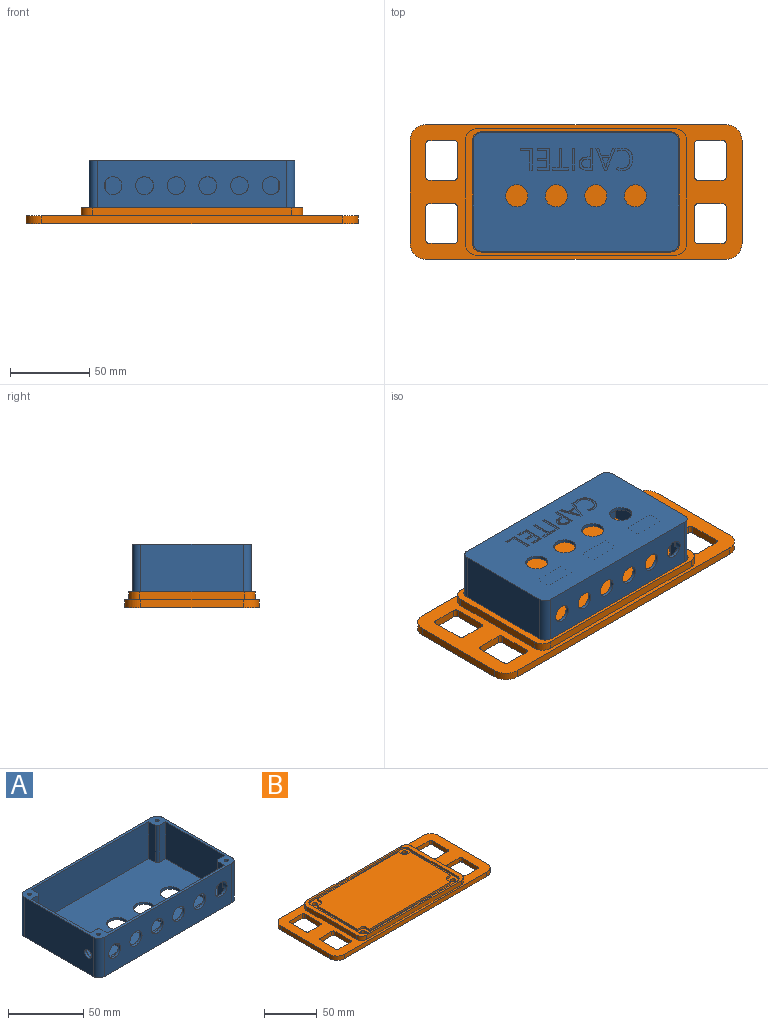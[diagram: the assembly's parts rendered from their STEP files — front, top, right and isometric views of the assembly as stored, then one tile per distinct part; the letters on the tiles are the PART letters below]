
ASSEMBLY  parts=2 mates=1
PART A: 147 faces, bbox 130x75x32 mm
  f0: plane 130x75mm, normal (0,0,-1), area 8800.8mm2, adj f16,f17,f18,f19,f20,f21,f22,f23
  f1: plane 9.5x1.5mm, normal (1,0,0), area 14.2mm2, adj f2,f4,f48,f64
  f2: plane 20.5x1.5mm, normal (0,-1,0), area 30.8mm2, adj f1,f3,f48,f64
  f3: plane 9.5x1.5mm, normal (-1,0,0), area 14.2mm2, adj f2,f4,f48,f64
  f4: plane 20.5x1.5mm, normal (0,1,0), area 30.8mm2, adj f1,f3,f48,f64
  f5: plane 9.5x1.5mm, normal (1,0,0), area 14.2mm2, adj f6,f8,f48,f63
  f6: plane 20.5x1.5mm, normal (0,-1,0), area 30.7mm2, adj f5,f7,f48,f63
  f7: plane 9.5x1.5mm, normal (-1,0,0), area 14.2mm2, adj f6,f8,f48,f63
  f8: plane 20.5x1.5mm, normal (0,1,0), area 30.7mm2, adj f5,f7,f48,f63
  f9: plane 9.5x1.5mm, normal (1,0,0), area 14.2mm2, adj f10,f12,f48,f62
  f10: plane 20.5x1.5mm, normal (0,-1,0), area 30.7mm2, adj f9,f11,f48,f62
  f11: plane 9.5x1.5mm, normal (-1,0,0), area 14.2mm2, adj f10,f12,f48,f62
  f12: plane 20.5x1.5mm, normal (0,1,0), area 30.7mm2, adj f9,f11,f48,f62
  f13: plane 10.75x6mm, normal (0,1,0), area 64.5mm2, adj f14,f33,f48,f61
  f14: cylinder r=2mm len=11.44mm, axis (0,0,-1), area 34.2mm2, adj f13,f36,f48,f61
  f15: plane 130x75mm, normal (0,0,1), area 1015.5mm2, adj f16,f17,f18,f19,f20,f21,f22,f23
  f16: cylinder r=5mm len=32mm, axis (0,0,-1), area 251.3mm2, adj f0,f15,f17,f23
  f17: plane 65x32mm, normal (-1,0,0), area 2046.8mm2, adj f0,f15,f16,f18,f61
  f18: cylinder r=5mm len=32mm, axis (0,0,-1), area 251.3mm2, adj f0,f15,f17,f19
  f19: plane 120x32mm, normal (0,-1,0), area 3238.3mm2, adj f0,f15,f18,f20,f49,f51,f52,f53
  f20: cylinder r=5mm len=32mm, axis (0,0,-1), area 251.3mm2, adj f0,f15,f19,f21
  f21: plane 65x32mm, normal (1,0,0), area 2080mm2, adj f0,f15,f20,f22
  f22: cylinder r=5mm len=32mm, axis (0,0,-1), area 251.3mm2, adj f0,f15,f21,f23
  f23: plane 120x32mm, normal (0,1,0), area 3840mm2, adj f0,f15,f16,f22
  f24: plane 30x6mm, normal (0,1,0), area 180mm2, adj f15,f25,f39,f48
  f25: plane 55x30mm, normal (-1,0,0), area 1650mm2, adj f15,f24,f26,f48
  f26: plane 30x6mm, normal (0,-1,0), area 180mm2, adj f15,f25,f27,f48
  f27: cylinder r=2mm len=30mm, axis (0,0,-1), area 94.2mm2, adj f15,f26,f28,f48
  f28: plane 30x6mm, normal (-1,0,0), area 180mm2, adj f15,f27,f29,f48
  f29: plane 110x30mm, normal (0,-1,0), area 3300mm2, adj f15,f28,f30,f48
  f30: plane 30x6mm, normal (1,0,0), area 180mm2, adj f15,f29,f31,f48
  f31: cylinder r=2mm len=30mm, axis (0,0,-1), area 94.2mm2, adj f15,f30,f32,f48
  f32: plane 30x6mm, normal (0,-1,0), area 180mm2, adj f15,f31,f33,f48
  f33: plane 55x30mm, normal (1,0,0), area 1633.4mm2, adj f13,f15,f32,f34,f48,f61
  f34: plane 12.75x6mm, normal (0,1,0), area 76.5mm2, adj f15,f33,f35,f61
  f35: cylinder r=2mm len=13.44mm, axis (0,0,-1), area 40.5mm2, adj f15,f34,f36,f61
  f36: plane 30x6mm, normal (1,0,0), area 165mm2, adj f14,f15,f35,f37,f48,f49,f50,f61
  f37: plane 110x30mm, normal (0,1,0), area 2702.9mm2, adj f15,f36,f38,f48,f49,f51,f52,f53
  f38: plane 30x6mm, normal (-1,0,0), area 169.5mm2, adj f15,f37,f39,f48,f55,f56
  f39: cylinder r=2mm len=30mm, axis (0,0,-1), area 94.2mm2, adj f15,f24,f38,f48
  f40: cylinder r=1.25mm len=30mm, axis (0,0,-1), area 235.6mm2, adj f15,f47
  f41: cylinder r=1.25mm len=30mm, axis (0,0,-1), area 235.6mm2, adj f15,f46
  f42: cylinder r=1.25mm len=30mm, axis (0,0,-1), area 235.6mm2, adj f15,f45
  f43: cylinder r=1.25mm len=30mm, axis (0,0,-1), area 235.6mm2, adj f15,f44
  f44: plane 2.5x2.5mm, normal (0,0,1), area 4.9mm2, adj f43
  f45: plane 2.5x2.5mm, normal (0,0,1), area 4.9mm2, adj f42
  f46: plane 2.5x2.5mm, normal (0,0,1), area 4.9mm2, adj f41
  f47: plane 2.5x2.5mm, normal (0,0,1), area 4.9mm2, adj f40
  f48: plane 126x71mm, normal (0,0,1), area 7493.4mm2, adj f1,f2,f3,f4,f5,f6,f7,f8
  f49: cylinder r=5.65mm len=11.3mm, axis (0,-1,0), area 81.9mm2, adj f19,f36,f37,f50
  f50: plane 5.26x0.65mm, normal (0,-1,0), area 2.3mm2, adj f36,f49
  f51: cylinder r=5.65mm len=11.3mm, axis (0,-1,0), area 71mm2, adj f19,f37
  f52: cylinder r=5.65mm len=11.3mm, axis (0,-1,0), area 71mm2, adj f19,f37
  f53: cylinder r=5.65mm len=11.3mm, axis (0,-1,0), area 71mm2, adj f19,f37
  f54: cylinder r=5.65mm len=11.3mm, axis (0,-1,0), area 71mm2, adj f19,f37
  f55: cylinder r=5.65mm len=11.3mm, axis (0,-1,0), area 81.9mm2, adj f19,f37,f38,f56
  f56: plane 5.26x0.65mm, normal (0,-1,0), area 2.3mm2, adj f38,f55
  f57: cylinder r=7mm len=14mm, axis (0,0,1), area 88mm2, adj f0,f48
  f58: cylinder r=7mm len=14mm, axis (0,0,1), area 88mm2, adj f0,f48
  f59: cylinder r=7mm len=14mm, axis (0,0,1), area 88mm2, adj f0,f48
  f60: cylinder r=7mm len=14mm, axis (0,0,1), area 88mm2, adj f0,f48
  f61: cylinder r=3.25mm len=10mm, axis (-1,0,0), area 120.8mm2, adj f13,f14,f17,f33,f34,f35,f36
  f62: plane 20.5x9.5mm, normal (0,0,1), area 194.7mm2, adj f9,f10,f11,f12
  f63: plane 20.5x9.5mm, normal (0,0,1), area 194.7mm2, adj f5,f6,f7,f8
  f64: plane 20.5x9.5mm, normal (0,0,1), area 194.8mm2, adj f1,f2,f3,f4
  f65: extruded ~5.16x4.01mm, area 3.7mm2, adj f0,f66,f79,f80
  f66: plane 3.57x0.5mm, normal (0,1,0), area 1.8mm2, adj f0,f65,f67,f80
  f67: plane 13.77x0.5mm, normal (1,0,0), area 6.9mm2, adj f0,f66,f68,f80
  f68: plane 1.6x0.5mm, normal (0,-1,0), area 0.8mm2, adj f0,f67,f69,f80
  f69: plane 5.41x0.5mm, normal (-1,0,0), area 2.7mm2, adj f0,f68,f70,f80
  f70: plane 1.62x0.5mm, normal (0,-1,0), area 0.8mm2, adj f0,f69,f71,f80
  f71: extruded ~4.08x1.13mm, area 2.2mm2, adj f0,f70,f79,f80
  f72: plane 5.59x0.5mm, normal (-1,0,0), area 2.8mm2, adj f73,f78,f80,f81
  f73: plane 1.79x0.5mm, normal (0,-1,0), area 0.9mm2, adj f72,f74,f80,f81
  f74: extruded ~2.79x0.67mm, area 1.5mm2, adj f73,f75,f80,f81
  f75: extruded ~2.03x0.89mm, area 1.2mm2, adj f74,f76,f80,f81
  f76: extruded ~2.21x0.95mm, area 1.2mm2, adj f75,f77,f80,f81
  f77: extruded ~3.08x0.69mm, area 1.6mm2, adj f76,f78,f80,f81
  f78: plane 1.44x0.5mm, normal (0,1,0), area 0.7mm2, adj f72,f77,f80,f81
  f79: extruded ~3.22x1.43mm, area 1.8mm2, adj f0,f65,f71,f80
  f80: plane 13.77x8.73mm, normal (0,0,-1), area 46.7mm2, adj f65,f66,f67,f68,f69,f70,f71,f72
  f81: plane 5.59x5.47mm, normal (0,0,-1), area 27.2mm2, adj f72,f73,f74,f75,f76,f77,f78
  f82: plane 1.66x0.5mm, normal (0,-1,0), area 0.8mm2, adj f0,f83,f94,f95
  f83: plane 13.82x5.41mm, normal (-0.93,0.36,0), area 7.4mm2, adj f0,f82,f84,f95
  f84: plane 1.35x0.5mm, normal (0,1,0), area 0.7mm2, adj f0,f83,f85,f95
  f85: plane 13.82x5.44mm, normal (0.93,0.37,0), area 7.4mm2, adj f0,f84,f86,f95
  f86: plane 1.62x0.5mm, normal (0,-1,0), area 0.8mm2, adj f0,f85,f87,f95
  f87: plane 4.38x1.69mm, normal (-0.93,-0.36,0), area 2.3mm2, adj f0,f86,f88,f95
  f88: plane 5.52x0.5mm, normal (0,-1,0), area 2.8mm2, adj f0,f87,f94,f95
  f89: plane 4.45x0.5mm, normal (0,1,0), area 2.2mm2, adj f90,f93,f95,f96
  f90: plane 4.27x1.62mm, normal (-0.94,-0.35,0), area 2.3mm2, adj f89,f91,f95,f96
  f91: extruded ~1.99x0.59mm, area 1mm2, adj f90,f92,f95,f96
  f92: extruded ~1.99x0.64mm, area 1mm2, adj f91,f93,f95,f96
  f93: plane 4.27x1.6mm, normal (0.94,-0.35,0), area 2.3mm2, adj f89,f92,f95,f96
  f94: plane 4.38x1.71mm, normal (0.93,-0.36,0), area 2.4mm2, adj f0,f82,f88,f95
  f95: plane 13.82x12.2mm, normal (0,0,-1), area 48.8mm2, adj f82,f83,f84,f85,f86,f87,f88,f89
  f96: plane 6.25x4.45mm, normal (0,0,-1), area 13.3mm2, adj f89,f90,f91,f92,f93
  f97: plane 7.67x0.5mm, normal (0,-1,0), area 3.8mm2, adj f0,f98,f102,f103
  f98: plane 1.45x0.5mm, normal (-1,0,0), area 0.7mm2, adj f0,f97,f99,f103
  f99: plane 6.07x0.5mm, normal (0,1,0), area 3mm2, adj f0,f98,f100,f103
  f100: plane 12.32x0.5mm, normal (-1,0,0), area 6.2mm2, adj f0,f99,f101,f103
  f101: plane 1.6x0.5mm, normal (0,1,0), area 0.8mm2, adj f0,f100,f102,f103
  f102: plane 13.77x0.5mm, normal (1,0,0), area 6.9mm2, adj f0,f97,f101,f103
  f103: plane 13.77x7.67mm, normal (0,0,-1), area 30.8mm2, adj f97,f98,f99,f100,f101,f102
  f104: plane 1.43x0.5mm, normal (-1,0,0), area 0.7mm2, adj f0,f105,f115,f116
  f105: plane 6.07x0.5mm, normal (0,1,0), area 3mm2, adj f0,f104,f106,f116
  f106: plane 5.06x0.5mm, normal (-1,0,0), area 2.5mm2, adj f0,f105,f107,f116
  f107: plane 5.71x0.5mm, normal (0,-1,0), area 2.9mm2, adj f0,f106,f108,f116
  f108: plane 1.41x0.5mm, normal (-1,0,0), area 0.7mm2, adj f0,f107,f109,f116
  f109: plane 5.71x0.5mm, normal (0,1,0), area 2.9mm2, adj f0,f108,f110,f116
  f110: plane 4.43x0.5mm, normal (-1,0,0), area 2.2mm2, adj f0,f109,f111,f116
  f111: plane 6.07x0.5mm, normal (0,-1,0), area 3mm2, adj f0,f110,f112,f116
  f112: plane 1.42x0.5mm, normal (-1,0,0), area 0.7mm2, adj f0,f111,f113,f116
  f113: plane 7.67x0.5mm, normal (0,1,0), area 3.8mm2, adj f0,f112,f114,f116
  f114: plane 13.77x0.5mm, normal (1,0,0), area 6.9mm2, adj f0,f113,f115,f116
  f115: plane 7.67x0.5mm, normal (0,-1,0), area 3.8mm2, adj f0,f104,f114,f116
  f116: plane 13.77x7.67mm, normal (0,0,-1), area 47.4mm2, adj f104,f105,f106,f107,f108,f109,f110,f111
  f117: plane 12.34x0.5mm, normal (-1,0,0), area 6.2mm2, adj f0,f118,f124,f125
  f118: plane 4.36x0.5mm, normal (0,-1,0), area 2.2mm2, adj f0,f117,f119,f125
  f119: plane 1.42x0.5mm, normal (-1,0,0), area 0.7mm2, adj f0,f118,f120,f125
  f120: plane 10.32x0.5mm, normal (0,1,0), area 5.2mm2, adj f0,f119,f121,f125
  f121: plane 1.42x0.5mm, normal (1,0,0), area 0.7mm2, adj f0,f120,f122,f125
  f122: plane 4.36x0.5mm, normal (0,-1,0), area 2.2mm2, adj f0,f121,f123,f125
  f123: plane 12.34x0.5mm, normal (1,0,0), area 6.2mm2, adj f0,f122,f124,f125
  f124: plane 1.6x0.5mm, normal (0,-1,0), area 0.8mm2, adj f0,f117,f123,f125
  f125: plane 13.77x10.32mm, normal (0,0,-1), area 34.4mm2, adj f117,f118,f119,f120,f121,f122,f123,f124
  f126: plane 1.6x0.5mm, normal (0,-1,0), area 0.8mm2, adj f0,f127,f129,f130
  f127: plane 13.77x0.5mm, normal (-1,0,0), area 6.9mm2, adj f0,f126,f128,f130
  f128: plane 1.6x0.5mm, normal (0,1,0), area 0.8mm2, adj f0,f127,f129,f130
  f129: plane 13.77x0.5mm, normal (1,0,0), area 6.9mm2, adj f0,f126,f128,f130
  f130: plane 13.77x1.6mm, normal (0,0,-1), area 22mm2, adj f126,f127,f128,f129
  f131: extruded ~3.13x0.73mm, area 1.6mm2, adj f0,f132,f145,f146
  f132: plane 1.37x0.68mm, normal (-0.9,-0.44,0), area 0.8mm2, adj f0,f131,f133,f146
  f133: extruded ~3.78x0.79mm, area 1.9mm2, adj f0,f132,f134,f146
  f134: extruded ~3.54x0.87mm, area 1.8mm2, adj f0,f133,f135,f146
  f135: extruded ~2.47x2.3mm, area 1.7mm2, adj f0,f134,f136,f146
  f136: extruded ~3.73x0.8mm, area 1.9mm2, adj f0,f135,f137,f146
  f137: extruded ~5.25x1.65mm, area 2.8mm2, adj f0,f136,f138,f146
  f138: extruded ~4.69x1.85mm, area 2.6mm2, adj f0,f137,f139,f146
  f139: extruded ~3.53x0.54mm, area 1.8mm2, adj f0,f138,f140,f146
  f140: plane 1.4x0.5mm, normal (-1,0,0), area 0.7mm2, adj f0,f139,f141,f146
  f141: extruded ~3.29x0.52mm, area 1.7mm2, adj f0,f140,f142,f146
  f142: extruded ~3.61x1.47mm, area 2mm2, adj f0,f141,f143,f146
  f143: extruded ~4.17x1.27mm, area 2.2mm2, adj f0,f142,f144,f146
  f144: extruded ~4.14x1.31mm, area 2.2mm2, adj f0,f143,f145,f146
  f145: extruded ~3.58x1.51mm, area 2mm2, adj f0,f131,f144,f146
  f146: plane 14.15x10.41mm, normal (0,0,-1), area 41.4mm2, adj f131,f132,f133,f134,f135,f136,f137,f138
PART B: 81 faces, bbox 210x85x10 mm
  f0: plane 210x85mm, normal (0,0,1), area 4620mm2, adj f2,f3,f4,f5,f6,f7,f8,f9
  f1: plane 210x85mm, normal (0,0,-1), area 15699.4mm2, adj f2,f3,f4,f5,f6,f7,f8,f9
  f2: cylinder r=10mm len=10mm, axis (0,0,-1), area 78.5mm2, adj f0,f1,f3,f9
  f3: plane 190x5mm, normal (0,1,0), area 950mm2, adj f0,f1,f2,f4
  f4: cylinder r=10mm len=10mm, axis (0,0,-1), area 78.5mm2, adj f0,f1,f3,f5
  f5: plane 65x5mm, normal (-1,0,0), area 325mm2, adj f0,f1,f4,f6
  f6: cylinder r=10mm len=10mm, axis (0,0,-1), area 78.5mm2, adj f0,f1,f5,f7
  f7: plane 190x5mm, normal (0,-1,0), area 950mm2, adj f0,f1,f6,f8
  f8: cylinder r=10mm len=10mm, axis (0,0,-1), area 78.5mm2, adj f0,f1,f7,f9
  f9: plane 65x5mm, normal (1,0,0), area 325mm2, adj f0,f1,f2,f8
  f10: cylinder r=2mm len=5mm, axis (0,0,-1), area 15.7mm2, adj f0,f1,f11,f17
  f11: plane 21x5mm, normal (1,0,0), area 105mm2, adj f0,f1,f10,f12
  f12: cylinder r=2mm len=5mm, axis (0,0,-1), area 15.7mm2, adj f0,f1,f11,f13
  f13: plane 16x5mm, normal (0,1,0), area 80mm2, adj f0,f1,f12,f14
  f14: cylinder r=2mm len=5mm, axis (0,0,-1), area 15.7mm2, adj f0,f1,f13,f15
  f15: plane 21x5mm, normal (-1,0,0), area 105mm2, adj f0,f1,f14,f16
  f16: cylinder r=2mm len=5mm, axis (0,0,-1), area 15.7mm2, adj f0,f1,f15,f17
  f17: plane 16x5mm, normal (0,-1,0), area 80mm2, adj f0,f1,f10,f16
  f18: cylinder r=2mm len=5mm, axis (0,0,-1), area 15.7mm2, adj f0,f1,f19,f25
  f19: plane 21x5mm, normal (-1,0,0), area 105mm2, adj f0,f1,f18,f20
  f20: cylinder r=2mm len=5mm, axis (0,0,-1), area 15.7mm2, adj f0,f1,f19,f21
  f21: plane 16x5mm, normal (0,-1,0), area 80mm2, adj f0,f1,f20,f22
  f22: cylinder r=2mm len=5mm, axis (0,0,-1), area 15.7mm2, adj f0,f1,f21,f23
  f23: plane 21x5mm, normal (1,0,0), area 105mm2, adj f0,f1,f22,f24
  f24: cylinder r=2mm len=5mm, axis (0,0,-1), area 15.7mm2, adj f0,f1,f23,f25
  f25: plane 16x5mm, normal (0,1,0), area 80mm2, adj f0,f1,f18,f24
  f26: cylinder r=2mm len=5mm, axis (0,0,-1), area 15.7mm2, adj f0,f1,f27,f33
  f27: plane 21x5mm, normal (-1,0,0), area 105mm2, adj f0,f1,f26,f28
  f28: cylinder r=2mm len=5mm, axis (0,0,-1), area 15.7mm2, adj f0,f1,f27,f29
  f29: plane 16x5mm, normal (0,-1,0), area 80mm2, adj f0,f1,f28,f30
  f30: cylinder r=2mm len=5mm, axis (0,0,-1), area 15.7mm2, adj f0,f1,f29,f31
  f31: plane 21x5mm, normal (1,0,0), area 105mm2, adj f0,f1,f30,f32
  f32: cylinder r=2mm len=5mm, axis (0,0,-1), area 15.7mm2, adj f0,f1,f31,f33
  f33: plane 16x5mm, normal (0,1,0), area 80mm2, adj f0,f1,f26,f32
  f34: cylinder r=2mm len=5mm, axis (0,0,-1), area 15.7mm2, adj f0,f1,f35,f41
  f35: plane 16x5mm, normal (0,-1,0), area 80mm2, adj f0,f1,f34,f36
  f36: cylinder r=2mm len=5mm, axis (0,0,-1), area 15.7mm2, adj f0,f1,f35,f37
  f37: plane 21x5mm, normal (1,0,0), area 105mm2, adj f0,f1,f36,f38
  f38: cylinder r=2mm len=5mm, axis (0,0,-1), area 15.7mm2, adj f0,f1,f37,f39
  f39: plane 16x5mm, normal (0,1,0), area 80mm2, adj f0,f1,f38,f40
  f40: cylinder r=2mm len=5mm, axis (0,0,-1), area 15.7mm2, adj f0,f1,f39,f41
  f41: plane 21x5mm, normal (-1,0,0), area 105mm2, adj f0,f1,f34,f40
  f42: cylinder r=2.5mm len=8mm, axis (0,0,-1), area 125.7mm2, adj f1,f63
  f43: cylinder r=2.5mm len=8mm, axis (0,0,-1), area 125.7mm2, adj f1,f63
  f44: cylinder r=2.5mm len=8mm, axis (0,0,-1), area 125.7mm2, adj f1,f63
  f45: cylinder r=2.5mm len=8mm, axis (0,0,-1), area 125.7mm2, adj f1,f63
  f46: cylinder r=7mm len=7mm, axis (0,0,-1), area 55mm2, adj f0,f47,f53,f54
  f47: plane 126x5mm, normal (0,-1,0), area 630mm2, adj f0,f46,f48,f54
  f48: cylinder r=7mm len=7mm, axis (0,0,-1), area 55mm2, adj f0,f47,f49,f54
  f49: plane 66x5mm, normal (1,0,0), area 330mm2, adj f0,f48,f50,f54
  f50: cylinder r=7mm len=7mm, axis (0,0,-1), area 55mm2, adj f0,f49,f51,f54
  f51: plane 126x5mm, normal (0,1,0), area 630mm2, adj f0,f50,f52,f54
  f52: cylinder r=7mm len=7mm, axis (0,0,-1), area 55mm2, adj f0,f51,f53,f54
  f53: plane 66x5mm, normal (-1,0,0), area 330mm2, adj f0,f46,f52,f54
  f54: plane 140x80mm, normal (0,0,1), area 1227.9mm2, adj f46,f47,f48,f49,f50,f51,f52,f53
  f55: cylinder r=5.5mm len=5.5mm, axis (0,0,1), area 17.3mm2, adj f54,f56,f62,f63
  f56: plane 120x2mm, normal (0,-1,0), area 240mm2, adj f54,f55,f57,f63
  f57: cylinder r=5.5mm len=5.5mm, axis (0,0,1), area 17.3mm2, adj f54,f56,f58,f63
  f58: plane 65x2mm, normal (-1,0,0), area 130mm2, adj f54,f57,f59,f63
  f59: cylinder r=5.5mm len=5.5mm, axis (0,0,1), area 17.3mm2, adj f54,f58,f60,f63
  f60: plane 120x2mm, normal (0,1,0), area 240mm2, adj f54,f59,f61,f63
  f61: cylinder r=5.5mm len=5.5mm, axis (0,0,1), area 17.3mm2, adj f54,f60,f62,f63
  f62: plane 65x2mm, normal (1,0,0), area 130mm2, adj f54,f55,f61,f63
  f63: plane 131x76mm, normal (0,0,1), area 1352.1mm2, adj f42,f43,f44,f45,f55,f56,f57,f58
  f64: plane 5.5x2mm, normal (0,1,0), area 11mm2, adj f63,f65,f79,f80
  f65: cylinder r=2.5mm len=2.5mm, axis (0,0,1), area 7.9mm2, adj f63,f64,f66,f80
  f66: plane 5.5x2mm, normal (-1,0,0), area 11mm2, adj f63,f65,f67,f80
  f67: plane 109x2mm, normal (0,1,0), area 218mm2, adj f63,f66,f68,f80
  f68: plane 5.5x2mm, normal (1,0,0), area 11mm2, adj f63,f67,f69,f80
  f69: cylinder r=2.5mm len=2.5mm, axis (0,0,1), area 7.9mm2, adj f63,f68,f70,f80
  f70: plane 5.5x2mm, normal (0,1,0), area 11mm2, adj f63,f69,f71,f80
  f71: plane 54x2mm, normal (1,0,0), area 108mm2, adj f63,f70,f72,f80
  f72: plane 5.5x2mm, normal (0,-1,0), area 11mm2, adj f63,f71,f73,f80
  f73: cylinder r=2.5mm len=2.5mm, axis (0,0,1), area 7.9mm2, adj f63,f72,f74,f80
  f74: plane 5.5x2mm, normal (1,0,0), area 11mm2, adj f63,f73,f75,f80
  f75: plane 109x2mm, normal (0,-1,0), area 218mm2, adj f63,f74,f76,f80
  f76: plane 5.5x2mm, normal (-1,0,0), area 11mm2, adj f63,f75,f77,f80
  f77: cylinder r=2.5mm len=2.5mm, axis (0,0,1), area 7.9mm2, adj f63,f76,f78,f80
  f78: plane 5.5x2mm, normal (0,-1,0), area 11mm2, adj f63,f77,f79,f80
  f79: plane 54x2mm, normal (-1,0,0), area 108mm2, adj f63,f64,f78,f80
  f80: plane 125x70mm, normal (0,0,1), area 8499.4mm2, adj f64,f65,f66,f67,f68,f69,f70,f71
PLACE A rot(axis=(0,1,0),180deg) t=(108.99,-12.07,33.05)mm
PLACE B t=(-61.01,-17.07,-4.95)mm
MATE fastened A.f20 <-> B.f43  axis (0,0,-1) through (-16.01,-7.07,3.05)mm
